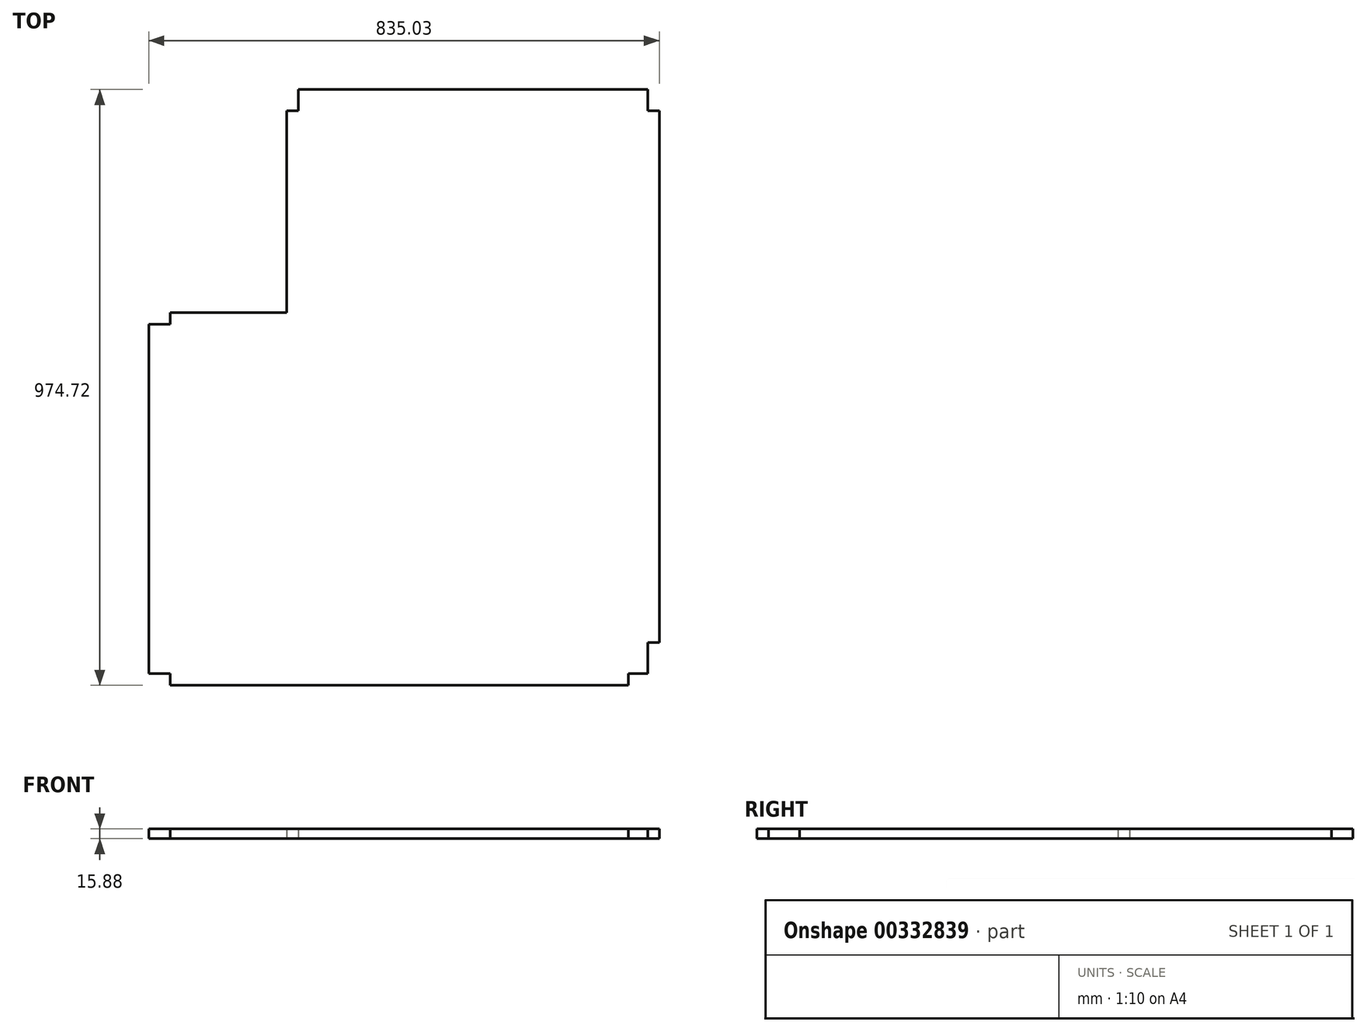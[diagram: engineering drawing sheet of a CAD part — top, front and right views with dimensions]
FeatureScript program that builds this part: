
annotation { "Feature Type Name" : "Feature", "Feature Type Description" : "" }
export const myFeature = defineFeature(function(context is Context, id is Id, definition is map)
    precondition{}
    {
        {
            var Q0;
            Q0=qCreatedBy(makeId("Top.planeOp"),FACE);
            var sketch = newSketch(context, id + "F0", { "sketchPlane" : qUnion([Q0])});
            skLineSegment(sketch, "E0.bottom", {"start": v(-31.75, 0) * mm, "end": v(-781.05, 0) * mm});
            skLineSegment(sketch, "E0.top", {"start": v(0, 974.72) * mm, "end": v(-571.5, 974.72) * mm});
            skLineSegment(sketch, "E0.left", {"start": v(19.05, 69.85) * mm, "end": v(19.05, 939.8) * mm});
            skLineSegment(sketch, "E1.right", {"start": v(-590.55, 939.8) * mm, "end": v(-590.55, 609.6) * mm});
            skLineSegment(sketch, "E2.top", {"start": v(-590.55, 939.8) * mm, "end": v(-571.5, 939.8) * mm});
            skLineSegment(sketch, "E2.right", {"start": v(-571.5, 974.72) * mm, "end": v(-571.5, 939.8) * mm});
            skLineSegment(sketch, "E3.top", {"start": v(19.05, 939.8) * mm, "end": v(0, 939.8) * mm});
            skLineSegment(sketch, "E3.right", {"start": v(0, 974.72) * mm, "end": v(0, 939.8) * mm});
            skLineSegment(sketch, "E4.top", {"start": v(-815.97, 590.55) * mm, "end": v(-781.05, 590.55) * mm});
            skLineSegment(sketch, "E4.right", {"start": v(-781.05, 609.6) * mm, "end": v(-781.05, 590.55) * mm});
            skLineSegment(sketch, "E5.trimOffspring", {"start": v(-781.05, 609.6) * mm, "end": v(-590.55, 609.6) * mm});
            skLineSegment(sketch, "E6.bottom", {"start": v(-815.97, 19.05) * mm, "end": v(-781.05, 19.05) * mm});
            skLineSegment(sketch, "E6.right", {"start": v(-781.05, 19.05) * mm, "end": v(-781.05, 0) * mm});
            skPoint(sketch, "E7.orphan", {"position": v(-781.05, -26.46) * mm});
            skLineSegment(sketch, "E8.top", {"start": v(0, 19.05) * mm, "end": v(-31.75, 19.05) * mm});
            skLineSegment(sketch, "E8.right", {"start": v(-31.75, 0) * mm, "end": v(-31.75, 19.05) * mm});
            skLineSegment(sketch, "E9.top", {"start": v(0, 69.85) * mm, "end": v(19.05, 69.85) * mm});
            skLineSegment(sketch, "E9.left", {"start": v(0, 19.05) * mm, "end": v(0, 69.85) * mm});
            skLineSegment(sketch, "E10", {"start": v(-815.97, 590.55) * mm, "end": v(-815.97, 19.05) * mm});
            skPoint(sketch, "E6.left.start.orphan", {"position": v(-850.9, 19.05) * mm});
            skPoint(sketch, "E4.left.end.orphan", {"position": v(-850.9, 590.55) * mm});
            skSolve(sketch);
        }
        {
            var Q0;
            Q0=qSketchRegion(id+"F0",true);
            extrude(context, id + "F1", {"entities" : qUnion([Q0]), "depth" : 15.88 * mm});
        }
    });
